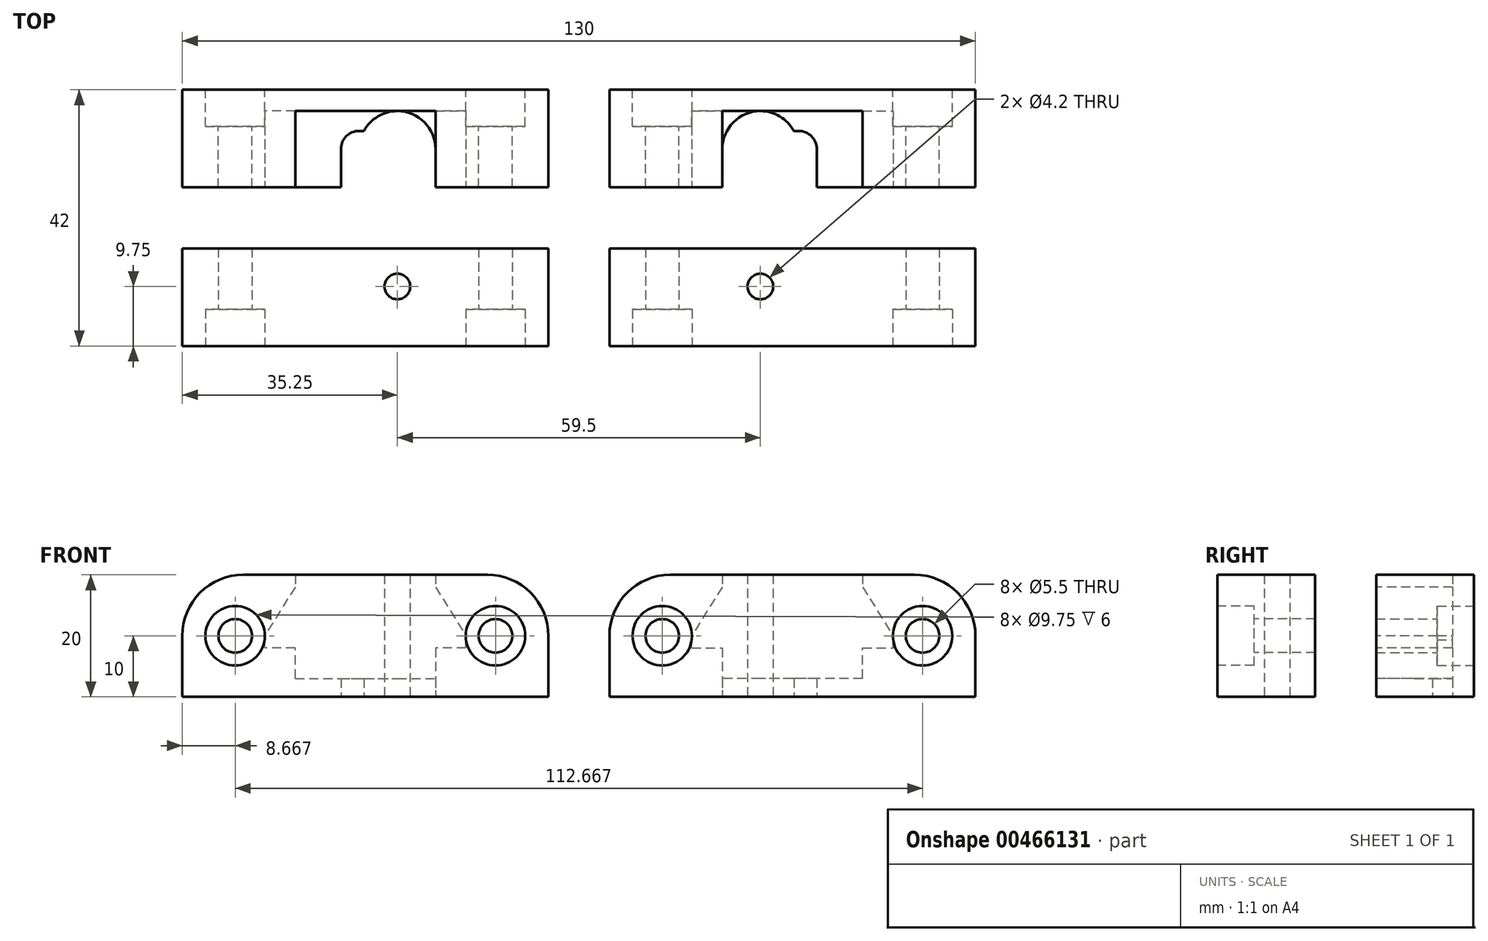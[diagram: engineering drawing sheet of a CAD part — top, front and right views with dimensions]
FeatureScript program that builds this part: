
annotation { "Feature Type Name" : "Feature", "Feature Type Description" : "" }
export const myFeature = defineFeature(function(context is Context, id is Id, definition is map)
    precondition{}
    {
        {
            var Q0;
            Q0=qCreatedBy(makeId("Top.planeOp"),FACE);
            var sketch = newSketch(context, id + "F0", { "sketchPlane" : qUnion([Q0])});
            skLineSegment(sketch, "E0.top", {"start": v(-30, 21) * mm, "end": v(30, 21) * mm});
            skLineSegment(sketch, "E0.left", {"start": v(-30, 5) * mm, "end": v(-30, 21) * mm});
            skLineSegment(sketch, "E0.right", {"start": v(30, 5) * mm, "end": v(30, 21) * mm});
            skLineSegment(sketch, "E1", {"start": v(-30, 5) * mm, "end": v(30, 5) * mm});
            skLineSegment(sketch, "E2.MirrorCS", {"start": v(-30, -5) * mm, "end": v(30, -5) * mm});
            skLineSegment(sketch, "E3.MirrorCS", {"start": v(-30, -5) * mm, "end": v(-30, -21) * mm});
            skLineSegment(sketch, "E4.MirrorCS", {"start": v(30, -5) * mm, "end": v(30, -21) * mm});
            skLineSegment(sketch, "E5.MirrorCS", {"start": v(-30, -21) * mm, "end": v(30, -21) * mm});
            skPoint(sketch, "E6.MirrorP", {"position": v(30, -21) * mm});
            skPoint(sketch, "E7.MirrorP", {"position": v(-30, -21) * mm});
            skSolve(sketch);
        }
        {
            var Q0;
            Q0=qSketchRegion(id+"F0",true);
            extrude(context, id + "F1", {"entities" : qUnion([Q0]), "depth" : 20 * mm, "offsetDistance" : 25 * mm});
        }
        {
            var Q0;
            Q0=makeQuery(id+"F1.opExtrude","SWEPT_FACE",FACE,{"disambiguationData":[OSD([sQuery(id+"F0.wireOp",EDGE,"E0.top")])]});
            var sketch = newSketch(context, id + "F2", { "sketchPlane" : qUnion([Q0])});
            skLineSegment(sketch, "E8", {"start": v(-21.33, 10) * mm, "end": v(21.33, 10) * mm, "construction": true});
            skSolve(sketch);
        }
        {
            var Q0;
            Q0=sQuery(id+"F2.wireOp",VERTEX,"E8.start");
            var Q1;
            Q1=sQuery(id+"F2.wireOp",VERTEX,"E8.end");
            var Q2;
            Q2=makeQuery(id+"F1.opExtrude","SWEPT_BODY",BODY,{"disambiguationData":[OSD([sQuery(id+"F0.wireOp",EDGE,"E0.top"),sQuery(id+"F0.wireOp",EDGE,"E0.left"),sQuery(id+"F0.wireOp",EDGE,"E0.right"),sQuery(id+"F0.wireOp",EDGE,"Gibb6dG3-mp1D-AHKF-jRVd-UPADP8Vj1Xy0.bottom"),sQuery(id+"F0.wireOp",EDGE,"Gibb6dG3-mp1D-AHKF-jRVd-UPADP8Vj1Xy0.left"),sQuery(id+"F0.wireOp",EDGE,"Gibb6dG3-mp1D-AHKF-jRVd-UPADP8Vj1Xy0.right"),sQuery(id+"F0.wireOp",EDGE,"hRMouZ4F-RLiD-t7vQ-tbI4-mRz4POqrihTT"),sQuery(id+"F0.wireOp",EDGE,"XOJjQQDG-g3ae-harn-Volr-CAwtbYXSsiBH"),sQuery(id+"F0.wireOp",EDGE,"5fd792df-5d17-4878-9ded-c7dbeebee632.filletArc"),sQuery(id+"F0.wireOp",EDGE,"280e86c7-1862-47f0-ac95-835da23f7d1a.filletArc")])]});
            hole(context, id + "F3", {"style" : HoleStyle.C_BORE, "endStyle" : HoleEndStyle.THROUGH, "holeDiameter" : 5.5 * mm, "cBoreDiameter" : 9.75 * mm, "cBoreDepth" : 6 * mm, "majorDiameter" : 5 * mm, "isTappedThrough" : true, "tappedDepth" : 12 * mm, "tapClearance" : 3, "startFromSketch" : true, "locations" : qUnion([Q0, Q1]), "scope" : qUnion([Q2])});
        }
        {
            var Q0;
            Q0=makeQuery(id+"F1.opExtrude","SWEPT_FACE",FACE,{"disambiguationData":[OSD([sQuery(id+"F0.wireOp",EDGE,"E1")])]});
            var sketch = newSketch(context, id + "F4", { "sketchPlane" : qUnion([Q0])});
            skLineSegment(sketch, "E9.left", {"start": v(16.5, 8) * mm, "end": v(16.5, 10) * mm});
            skLineSegment(sketch, "E9.right", {"start": v(-16.5, 8) * mm, "end": v(-16.5, 10) * mm});
            skLineSegment(sketch, "E10.bottom", {"start": v(11.5, 3) * mm, "end": v(-11.5, 3) * mm});
            skLineSegment(sketch, "E11", {"start": v(-16.5, 8) * mm, "end": v(-11.5, 8) * mm});
            skLineSegment(sketch, "E12", {"start": v(-11.5, 8) * mm, "end": v(-11.5, 3) * mm});
            skLineSegment(sketch, "E13", {"start": v(11.5, 3) * mm, "end": v(11.5, 8) * mm});
            skLineSegment(sketch, "E14", {"start": v(11.5, 8) * mm, "end": v(16.5, 8) * mm});
            skLineSegment(sketch, "E15", {"start": v(-11.5, 21) * mm, "end": v(-11.5, 18) * mm});
            skLineSegment(sketch, "E16", {"start": v(-11.5, 18) * mm, "end": v(-16.5, 10) * mm});
            skLineSegment(sketch, "E17", {"start": v(11.5, 18) * mm, "end": v(16.5, 10) * mm});
            skLineSegment(sketch, "E18", {"start": v(11.5, 21) * mm, "end": v(11.5, 18) * mm});
            skLineSegment(sketch, "E19", {"start": v(11.5, 21) * mm, "end": v(-11.5, 21) * mm});
            skSolve(sketch);
        }
        {
            var Q0;
            Q0=makeQuery(id+"F4.imprint","IMPRINT",FACE,{"disambiguationData":[TD([[makeQuery(id+"F4.imprint","IMPRINT",EDGE,{"derivedFrom":sQuery(id+"F4.wireOp",EDGE,"E9.left")}),1.0]])]});
            extrude(context, id + "F5", {"entities" : qUnion([Q0]), "operationType" : NewBodyOperationType.REMOVE, "oppositeDirection" : true, "depth" : 12.5 * mm, "offsetDistance" : 25 * mm});
        }
        {
            var Q0;
            Q0=makeQuery(id+"F1.opExtrude","CAP_FACE",FACE,{"disambiguationData":[OSD([sQuery(id+"F0.wireOp",EDGE,"E0.top"),sQuery(id+"F0.wireOp",EDGE,"E0.left"),sQuery(id+"F0.wireOp",EDGE,"E0.right"),sQuery(id+"F0.wireOp",EDGE,"5fd792df-5d17-4878-9ded-c7dbeebee632.filletArc"),sQuery(id+"F0.wireOp",EDGE,"280e86c7-1862-47f0-ac95-835da23f7d1a.filletArc"),sQuery(id+"F0.wireOp",EDGE,"E1")])],"isStart":true});
            var sketch = newSketch(context, id + "F6", { "sketchPlane" : qUnion([Q0])});
            skCircle(sketch, "E20", {"center": v(-5.25, -11.25) * mm, "radius": 6.25 * mm, "construction": true});
            skCircle(sketch, "E21", {"center": v(1, -11.25) * mm, "radius": 3 * mm, "construction": true});
            skLineSegment(sketch, "E22", {"start": v(-11.5, -11.25) * mm, "end": v(-11.5, -4) * mm});
            skLineSegment(sketch, "E23", {"start": v(4, -11.25) * mm, "end": v(4, -4) * mm});
            skLineSegment(sketch, "E24", {"start": v(4, -4) * mm, "end": v(-11.5, -4) * mm});
            skLineSegment(sketch, "E25", {"start": v(1, -14.25) * mm, "end": v(0.23, -14.25) * mm});
            skArc(sketch, "E26", {"start": v(-11.5, -11.25) * mm, "mid": v(-6.8, -17.3) * mm, "end": v(0.23, -14.25) * mm});
            skArc(sketch, "E27", {"start": v(1, -14.25) * mm, "mid": v(3.12, -13.37) * mm, "end": v(4, -11.25) * mm});
            skLineSegment(sketch, "E28", {"start": v(-5.25, -11.25) * mm, "end": v(-5.25, 11.25) * mm, "construction": true});
            skSolve(sketch);
        }
        {
            var Q0;
            Q0=qSketchRegion(id+"F6",true);
            var Q1;
            Q1=makeQuery(id+"F5.boolean.opBoolean","COPY",FACE,{"derivedFrom":makeQuery(id+"F5.opExtrude","SWEPT_FACE",FACE,{"disambiguationData":[OSD([sQuery(id+"F4.wireOp",EDGE,"E10.bottom")])]})});
            extrude(context, id + "F7", {"entities" : qUnion([Q0]), "operationType" : NewBodyOperationType.REMOVE, "endBound" : BoundingType.UP_TO_SURFACE, "oppositeDirection" : true, "depth" : 25 * mm, "endBoundEntityFace" : qUnion([Q1]), "offsetDistance" : 25 * mm});
        }
        {
            var Q0;
            Q0=makeQuery(id+"F1.opExtrude","SWEPT_FACE",FACE,{"disambiguationData":[OSD([sQuery(id+"F0.wireOp",EDGE,"E5.MirrorCS")])]});
            var sketch = newSketch(context, id + "F8", { "sketchPlane" : qUnion([Q0])});
            skLineSegment(sketch, "E29", {"start": v(-21.33, 10) * mm, "end": v(21.33, 10) * mm, "construction": true});
            skSolve(sketch);
        }
        {
            var Q0;
            Q0=sQuery(id+"F8.wireOp",VERTEX,"E29.start");
            var Q1;
            Q1=sQuery(id+"F8.wireOp",VERTEX,"E29.end");
            var Q2;
            Q2=makeQuery(id+"F1.opExtrude","SWEPT_BODY",BODY,{"disambiguationData":[OSD([sQuery(id+"F0.wireOp",EDGE,"E2.MirrorCS"),sQuery(id+"F0.wireOp",EDGE,"E3.MirrorCS"),sQuery(id+"F0.wireOp",EDGE,"E4.MirrorCS"),sQuery(id+"F0.wireOp",EDGE,"E5.MirrorCS"),sQuery(id+"F0.wireOp",EDGE,"e3919fe6-d821-4119-9f4e-e16b424154c35.MirrorCS"),sQuery(id+"F0.wireOp",EDGE,"e3919fe6-d821-4119-9f4e-e16b424154c36.MirrorCS")])]});
            hole(context, id + "F9", {"style" : HoleStyle.C_BORE, "endStyle" : HoleEndStyle.THROUGH, "holeDiameter" : 5.5 * mm, "cBoreDiameter" : 9.75 * mm, "cBoreDepth" : 6 * mm, "majorDiameter" : 5 * mm, "isTappedThrough" : true, "tappedDepth" : 12 * mm, "tapClearance" : 3, "startFromSketch" : true, "locations" : qUnion([Q0, Q1]), "scope" : qUnion([Q2])});
        }
        {
            var Q0;
            Q0=sQuery(id+"F6.wireOp",VERTEX,"E28.end");
            var Q1;
            Q1=makeQuery(id+"F1.opExtrude","SWEPT_BODY",BODY,{"disambiguationData":[OSD([sQuery(id+"F0.wireOp",EDGE,"E2.MirrorCS"),sQuery(id+"F0.wireOp",EDGE,"E3.MirrorCS"),sQuery(id+"F0.wireOp",EDGE,"E4.MirrorCS"),sQuery(id+"F0.wireOp",EDGE,"E5.MirrorCS"),sQuery(id+"F0.wireOp",EDGE,"e3919fe6-d821-4119-9f4e-e16b424154c35.MirrorCS"),sQuery(id+"F0.wireOp",EDGE,"e3919fe6-d821-4119-9f4e-e16b424154c36.MirrorCS")])]});
            hole(context, id + "F10", {"style" : HoleStyle.SIMPLE, "endStyle" : HoleEndStyle.THROUGH, "standardTappedOrClearance" : lookupTablePath({ "standard" : "ISO", "engagement" : "75%", "pitch" : "0.8 mm", "size" : "M5", "type" : "Tapped" }), "standardBlindInLast" : lookupTablePath({ "standard" : "ISO", "engagement" : "75%", "pitch" : "0.8 mm", "size" : "M5", "type" : "Tapped" }), "holeDiameter" : 4.2 * mm, "majorDiameter" : 5 * mm, "showTappedDepth" : true, "isTappedThrough" : true, "tappedDepth" : 145.24 * mm, "tapClearance" : 3, "locations" : qUnion([Q0]), "scope" : qUnion([Q1])});
        }
        {
            var Q0;
            Q0=makeQuery(id+"F1.opExtrude","SWEPT_BODY",BODY,{"disambiguationData":[OSD([sQuery(id+"F0.wireOp",EDGE,"E2.MirrorCS"),sQuery(id+"F0.wireOp",EDGE,"E3.MirrorCS"),sQuery(id+"F0.wireOp",EDGE,"E4.MirrorCS"),sQuery(id+"F0.wireOp",EDGE,"E5.MirrorCS"),sQuery(id+"F0.wireOp",EDGE,"e3919fe6-d821-4119-9f4e-e16b424154c35.MirrorCS"),sQuery(id+"F0.wireOp",EDGE,"e3919fe6-d821-4119-9f4e-e16b424154c36.MirrorCS")])]});
            var Q1;
            Q1=makeQuery(id+"F1.opExtrude","SWEPT_BODY",BODY,{"disambiguationData":[OSD([sQuery(id+"F0.wireOp",EDGE,"E0.top"),sQuery(id+"F0.wireOp",EDGE,"E0.left"),sQuery(id+"F0.wireOp",EDGE,"E0.right"),sQuery(id+"F0.wireOp",EDGE,"5fd792df-5d17-4878-9ded-c7dbeebee632.filletArc"),sQuery(id+"F0.wireOp",EDGE,"280e86c7-1862-47f0-ac95-835da23f7d1a.filletArc"),sQuery(id+"F0.wireOp",EDGE,"E1")])]});
            var Q2;
            Q2=qCreatedBy(makeId("Right.planeOp"),FACE);
            mirror(context, id + "F11", {"entities" : qUnion([Q0, Q1]), "mirrorPlane" : qUnion([Q2])});
        }
        {
            var Q0;
            Q0=makeQuery(id+"F11.opPattern","COPY",BODY,{"derivedFrom":makeQuery(id+"F1.opExtrude","SWEPT_BODY",BODY,{"disambiguationData":[OSD([sQuery(id+"F0.wireOp",EDGE,"E0.top"),sQuery(id+"F0.wireOp",EDGE,"E0.left"),sQuery(id+"F0.wireOp",EDGE,"E0.right"),sQuery(id+"F0.wireOp",EDGE,"5fd792df-5d17-4878-9ded-c7dbeebee632.filletArc"),sQuery(id+"F0.wireOp",EDGE,"280e86c7-1862-47f0-ac95-835da23f7d1a.filletArc"),sQuery(id+"F0.wireOp",EDGE,"E1")])]}),"instanceName":"1"});
            var Q1;
            Q1=makeQuery(id+"F11.opPattern","COPY",BODY,{"derivedFrom":makeQuery(id+"F1.opExtrude","SWEPT_BODY",BODY,{"disambiguationData":[OSD([sQuery(id+"F0.wireOp",EDGE,"E2.MirrorCS"),sQuery(id+"F0.wireOp",EDGE,"E3.MirrorCS"),sQuery(id+"F0.wireOp",EDGE,"E4.MirrorCS"),sQuery(id+"F0.wireOp",EDGE,"E5.MirrorCS"),sQuery(id+"F0.wireOp",EDGE,"e3919fe6-d821-4119-9f4e-e16b424154c35.MirrorCS"),sQuery(id+"F0.wireOp",EDGE,"e3919fe6-d821-4119-9f4e-e16b424154c36.MirrorCS")])]}),"instanceName":"1"});
            var Q2;
            Q2=makeQuery(id+"F1.opExtrude","CAP_EDGE",EDGE,{"disambiguationData":[OSD([sQuery(id+"F0.wireOp",EDGE,"E5.MirrorCS")])],"isStart":true});
            transform(context, id + "F12", {"entities" : qUnion([Q0, Q1]), "transformType" : TransformType.TRANSLATION_3D, "dx" : -70 * mm, "dy" : 0 * mm, "dz" : 0 * mm, "makeCopy" : false});
        }
        {
            var Q0;
            Q0=makeQuery(id+"F1.opExtrude","CAP_EDGE",EDGE,{"disambiguationData":[OSD([sQuery(id+"F0.wireOp",EDGE,"E4.MirrorCS")])],"isStart":false});
            var Q1;
            Q1=makeQuery(id+"F1.opExtrude","CAP_EDGE",EDGE,{"disambiguationData":[OSD([sQuery(id+"F0.wireOp",EDGE,"E0.right")])],"isStart":false});
            var Q2;
            Q2=makeQuery(id+"F1.opExtrude","CAP_EDGE",EDGE,{"disambiguationData":[OSD([sQuery(id+"F0.wireOp",EDGE,"E0.left")])],"isStart":false});
            var Q3;
            Q3=makeQuery(id+"F1.opExtrude","CAP_EDGE",EDGE,{"disambiguationData":[OSD([sQuery(id+"F0.wireOp",EDGE,"E3.MirrorCS")])],"isStart":false});
            var Q4;
            Q4=makeQuery(id+"F11.opPattern","COPY",EDGE,{"derivedFrom":makeQuery(id+"F1.opExtrude","CAP_EDGE",EDGE,{"disambiguationData":[OSD([sQuery(id+"F0.wireOp",EDGE,"E3.MirrorCS")])],"isStart":false}),"instanceName":"1"});
            var Q5;
            Q5=makeQuery(id+"F11.opPattern","COPY",EDGE,{"derivedFrom":makeQuery(id+"F1.opExtrude","CAP_EDGE",EDGE,{"disambiguationData":[OSD([sQuery(id+"F0.wireOp",EDGE,"E0.left")])],"isStart":false}),"instanceName":"1"});
            var Q6;
            Q6=makeQuery(id+"F11.opPattern","COPY",EDGE,{"derivedFrom":makeQuery(id+"F1.opExtrude","CAP_EDGE",EDGE,{"disambiguationData":[OSD([sQuery(id+"F0.wireOp",EDGE,"E0.right")])],"isStart":false}),"instanceName":"1"});
            var Q7;
            Q7=makeQuery(id+"F11.opPattern","COPY",EDGE,{"derivedFrom":makeQuery(id+"F1.opExtrude","CAP_EDGE",EDGE,{"disambiguationData":[OSD([sQuery(id+"F0.wireOp",EDGE,"E4.MirrorCS")])],"isStart":false}),"instanceName":"1"});
            fillet(context, id + "F13", {"entities" : qUnion([Q0, Q1, Q2, Q3, Q4, Q5, Q6, Q7]), "radius" : 10 * mm, "tangentPropagation" : true, "allowEdgeOverflow" : false});
        }
    });
